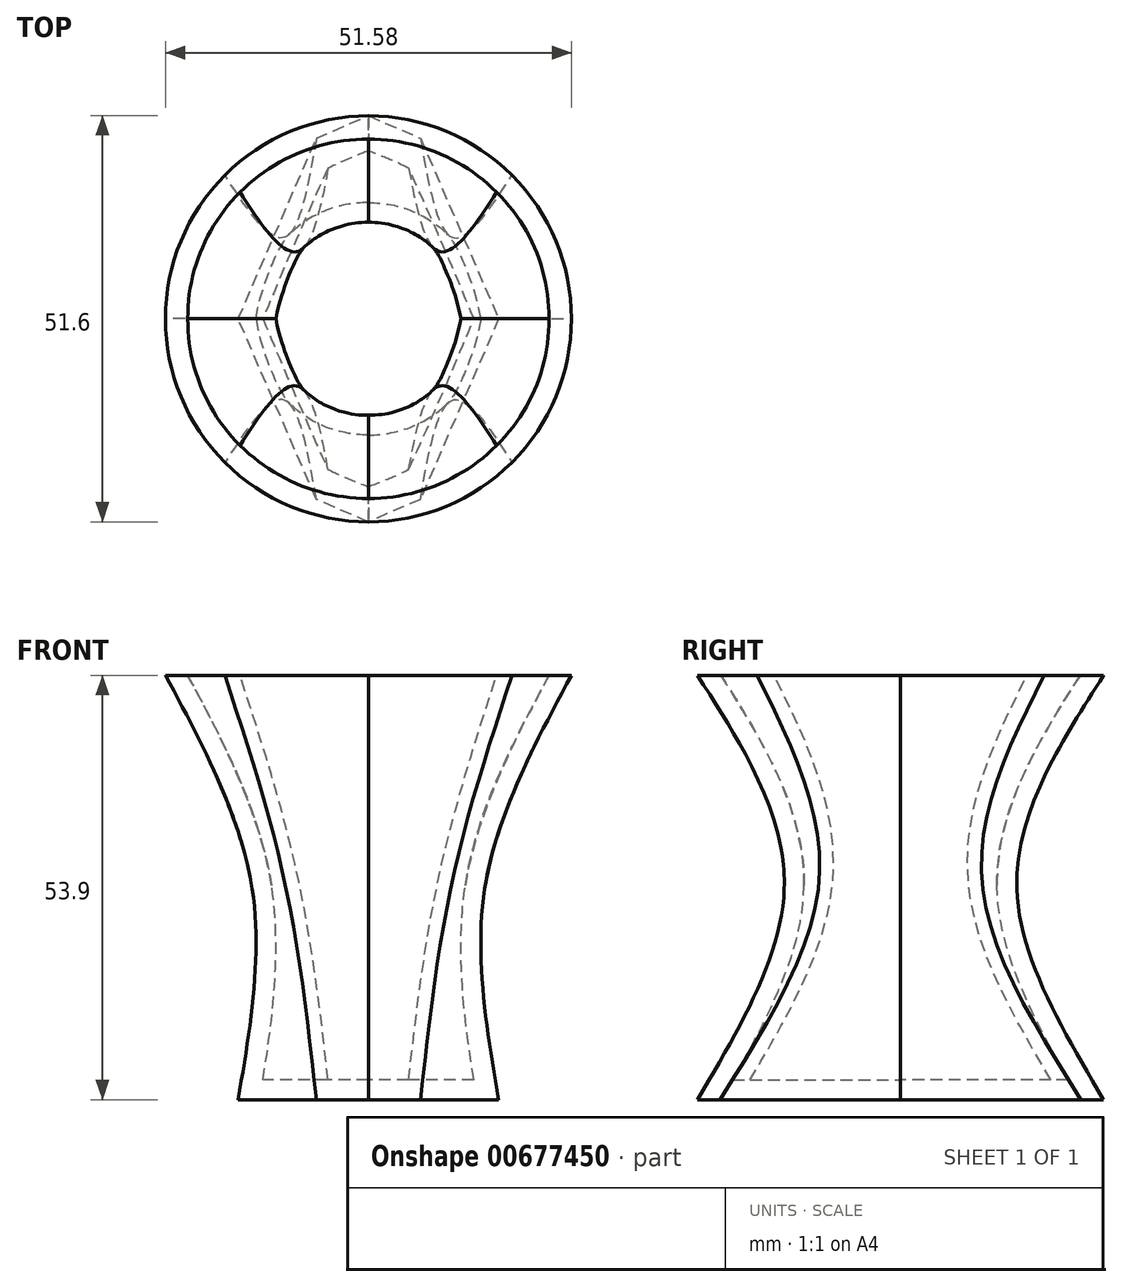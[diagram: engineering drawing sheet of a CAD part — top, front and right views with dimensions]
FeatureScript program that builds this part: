
annotation { "Feature Type Name" : "Feature", "Feature Type Description" : "" }
export const myFeature = defineFeature(function(context is Context, id is Id, definition is map)
    precondition{}
    {
        {
            var Q0;
            Q0=qCreatedBy(makeId("Top.planeOp"),FACE);
            cPlane(context, id + "F0", {"entities" : qUnion([Q0]), "cplaneType" : CPlaneType.OFFSET, "offset" : 53.9 * mm, "width" : 150 * mm, "height" : 150 * mm});
        }
        {
            var Q0;
            Q0=qCreatedBy(makeId("Top.planeOp"),FACE);
            var sketch = newSketch(context, id + "F1", { "sketchPlane" : qUnion([Q0])});
            skLineSegment(sketch, "E0", {"start": v(-16.55, 0) * mm, "end": v(-6.6, 22.94) * mm});
            skLineSegment(sketch, "E1", {"start": v(-6.6, 22.94) * mm, "end": v(0, 25.8) * mm});
            skLineSegment(sketch, "E2", {"start": v(0, 25.8) * mm, "end": v(6.6, 22.94) * mm});
            skLineSegment(sketch, "E3", {"start": v(6.6, 22.94) * mm, "end": v(16.55, 0) * mm});
            skLineSegment(sketch, "E4", {"start": v(16.55, 0) * mm, "end": v(6.6, -22.94) * mm});
            skLineSegment(sketch, "E5", {"start": v(6.6, -22.94) * mm, "end": v(0, -25.8) * mm});
            skLineSegment(sketch, "E6", {"start": v(0, -25.8) * mm, "end": v(-6.6, -22.94) * mm});
            skLineSegment(sketch, "E7", {"start": v(-6.6, -22.94) * mm, "end": v(-16.55, 0) * mm});
            skSolve(sketch);
        }
        {
            var Q0;
            Q0=qCreatedBy(id+"F0.planeOp",FACE);
            var sketch = newSketch(context, id + "F2", { "sketchPlane" : qUnion([Q0])});
            skCircle(sketch, "E8", {"center": v(0, 0) * mm, "radius": 25.79 * mm});
            skLineSegment(sketch, "E9", {"start": v(-0.18, 25.79) * mm, "end": v(-0.6, 25.79) * mm});
            skSolve(sketch);
        }
        {
            var Q0;
            Q0=qCreatedBy(makeId("Top.planeOp"),FACE);
            cPlane(context, id + "F3", {"entities" : qUnion([Q0]), "cplaneType" : CPlaneType.OFFSET, "offset" : 26.8 * mm, "width" : 150 * mm, "height" : 150 * mm});
        }
        {
            var Q0;
            Q0=qCreatedBy(id+"F3.planeOp",FACE);
            var sketch = newSketch(context, id + "F4", { "sketchPlane" : qUnion([Q0])});
            skCircle(sketch, "E10", {"center": v(0, 0) * mm, "radius": 14.77 * mm});
            skSolve(sketch);
        }
        {
            var Q0;
            Q0=makeQuery(id+"F1.imprint","IMPRINT",FACE,{"disambiguationData":[TD([[makeQuery(id+"F1.imprint","IMPRINT",EDGE,{"derivedFrom":sQuery(id+"F1.wireOp",EDGE,"E0")}),-1.0]])]});
            var Q1;
            Q1=makeQuery(id+"F4.imprint","IMPRINT",FACE,{"disambiguationData":[TD([[makeQuery(id+"F4.imprint","IMPRINT",EDGE,{"derivedFrom":sQuery(id+"F4.wireOp",EDGE,"E10")}),1.0]])]});
            var Q2;
            {var subQ0=sQuery(id+"F2.wireOp",EDGE,"E8");Q2=makeQuery(id+"F2.imprint","IMPRINT",FACE,{"disambiguationData":[TD([[makeQuery(id+"F2.imprint","IMPRINT",EDGE,{"disambiguationData":[TD([[makeQuery(id+"F2.imprint","IMPRINT",VERTEX,{"derivedFrom":subQ0}),-1.0]])],"derivedFrom":subQ0}),1.0]])]});}
            loft(context, id + "F5", {"sheetProfilesArray" : [{ "sheetProfileEntities" : qUnion([Q0]) }, { "sheetProfileEntities" : qUnion([Q1]) }, { "sheetProfileEntities" : qUnion([Q2]) }]});
        }
        {
            var Q0;
            {var subQ0=sQuery(id+"F2.wireOp",EDGE,"E8");Q0=makeQuery(id+"F5.opLoft","CAP_FACE",FACE,{"disambiguationData":[OSD([makeQuery(id+"F2.imprint","IMPRINT",FACE,{"disambiguationData":[TD([[makeQuery(id+"F2.imprint","IMPRINT",EDGE,{"disambiguationData":[TD([[makeQuery(id+"F2.imprint","IMPRINT",VERTEX,{"derivedFrom":subQ0}),-1.0]])],"derivedFrom":subQ0}),1.0]])]})])],"isStart":true});}
            shell(context, id + "F6", {"entities" : qUnion([Q0]), "thickness" : 2.5 * mm});
        }
    });
